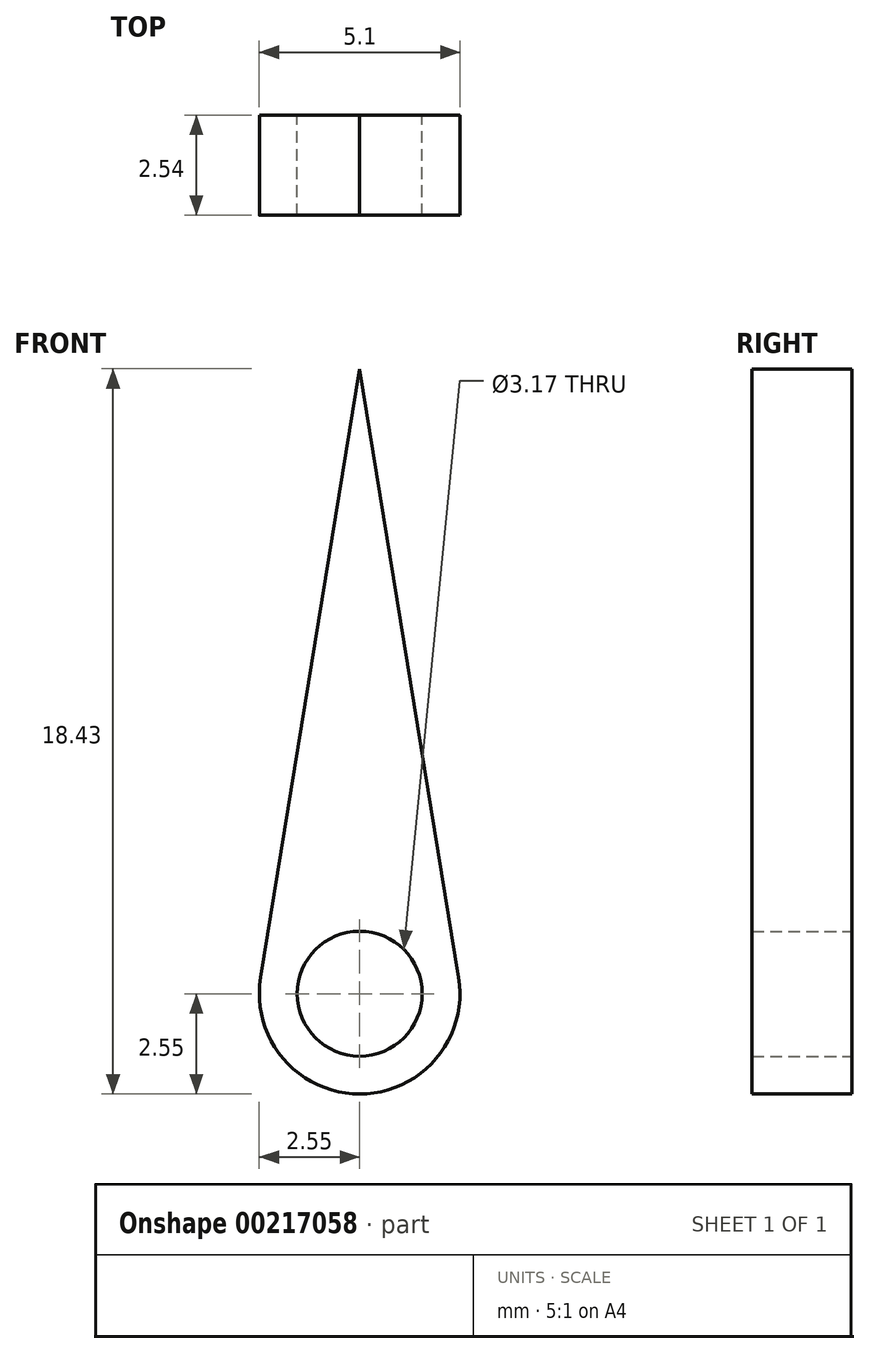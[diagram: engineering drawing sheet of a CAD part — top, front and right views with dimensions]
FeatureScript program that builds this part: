
annotation { "Feature Type Name" : "Feature", "Feature Type Description" : "" }
export const myFeature = defineFeature(function(context is Context, id is Id, definition is map)
    precondition{}
    {
        {
            var Q0;
            Q0=qCreatedBy(makeId("Front.planeOp"),FACE);
            var sketch = newSketch(context, id + "F0", { "sketchPlane" : qUnion([Q0])});
            skCircle(sketch, "E0", {"center": v(0, 0) * mm, "radius": 1.59 * mm});
            skCircle(sketch, "E1", {"center": v(0, 0) * mm, "radius": 2.55 * mm});
            skLineSegment(sketch, "E2", {"start": v(0, 15.88) * mm, "end": v(-2.58, 0) * mm});
            skLineSegment(sketch, "E3", {"start": v(0, 15.88) * mm, "end": v(2.58, 0) * mm});
            skSolve(sketch);
        }
        {
            var Q0;
            Q0=makeQuery(id+"F0.imprint","IMPRINT",FACE,{"disambiguationData":[TD([[makeQuery(id+"F0.imprint","IMPRINT",EDGE,{"derivedFrom":sQuery(id+"F0.wireOp",EDGE,"E0")}),-1.0]])]});
            extrude(context, id + "F1", {"entities" : qUnion([Q0]), "depth" : 2.54 * mm, "symmetric" : true});
        }
        {
            var Q0;
            {var subQ0=sQuery(id+"F0.wireOp",EDGE,"E2");var subQ1=sQuery(id+"F0.wireOp",EDGE,"E1");var subQ2=makeQuery(id+"F0.imprint","INTERSECT",VERTEX,{"derivedFrom":[subQ1,subQ0]});Q0=makeQuery(id+"F0.imprint","IMPRINT",FACE,{"disambiguationData":[TD([[makeQuery(id+"F0.imprint","IMPRINT",EDGE,{"disambiguationData":[TD([[subQ2,1.0]])],"derivedFrom":subQ1}),-1.0]])]});}
            extrude(context, id + "F2", {"entities" : qUnion([Q0]), "operationType" : NewBodyOperationType.ADD, "depth" : 2.54 * mm, "symmetric" : true});
        }
    });
